# Revit family: FU_Outdoor_Sandler_Zero 208
name_source: partatom
category: Furniture
units: mm (PartAtom-declared; Revit-internal decimal feet)

## family parameters
Always vertical = Yes
Cut with Voids When Loaded = No
OmniClass Number = 23.40.20.00
OmniClass Title = General Furniture and Specialties
Room Calculation Point = No
Shared = No
Work Plane-Based = No

## types (1)
- Zero 208
    Default Elevation = 0 mm  [stored 0 ft]
    Depth = 690 mm  [stored 2.26378 ft]
    Description = Upholstered sofa unit on a steel base, suitable for Outdoor. Stacks up to 4 with cushions removed. COM fabric needs to be outdoor treated for use on Zero, linking clips included.
    Frame = Metal - Paint - AL VR - Ruby Red
    Height = 800 mm  [stored 2.62467 ft]
    Manufacturer = Sandler
    Model = Zero 208
    Seat = Fabric - Outdoor - FabThirty 30319-18
    URL = https://www.sandlerseating.com
    Width = 600 mm

note: [stored X ft] marks values corroborated as IEEE doubles in the binary element streams (Revit-internal decimal feet)

## geometry (parser evidence)
native form markers: Sweep x3
no freeform markers — native parametric forms only
